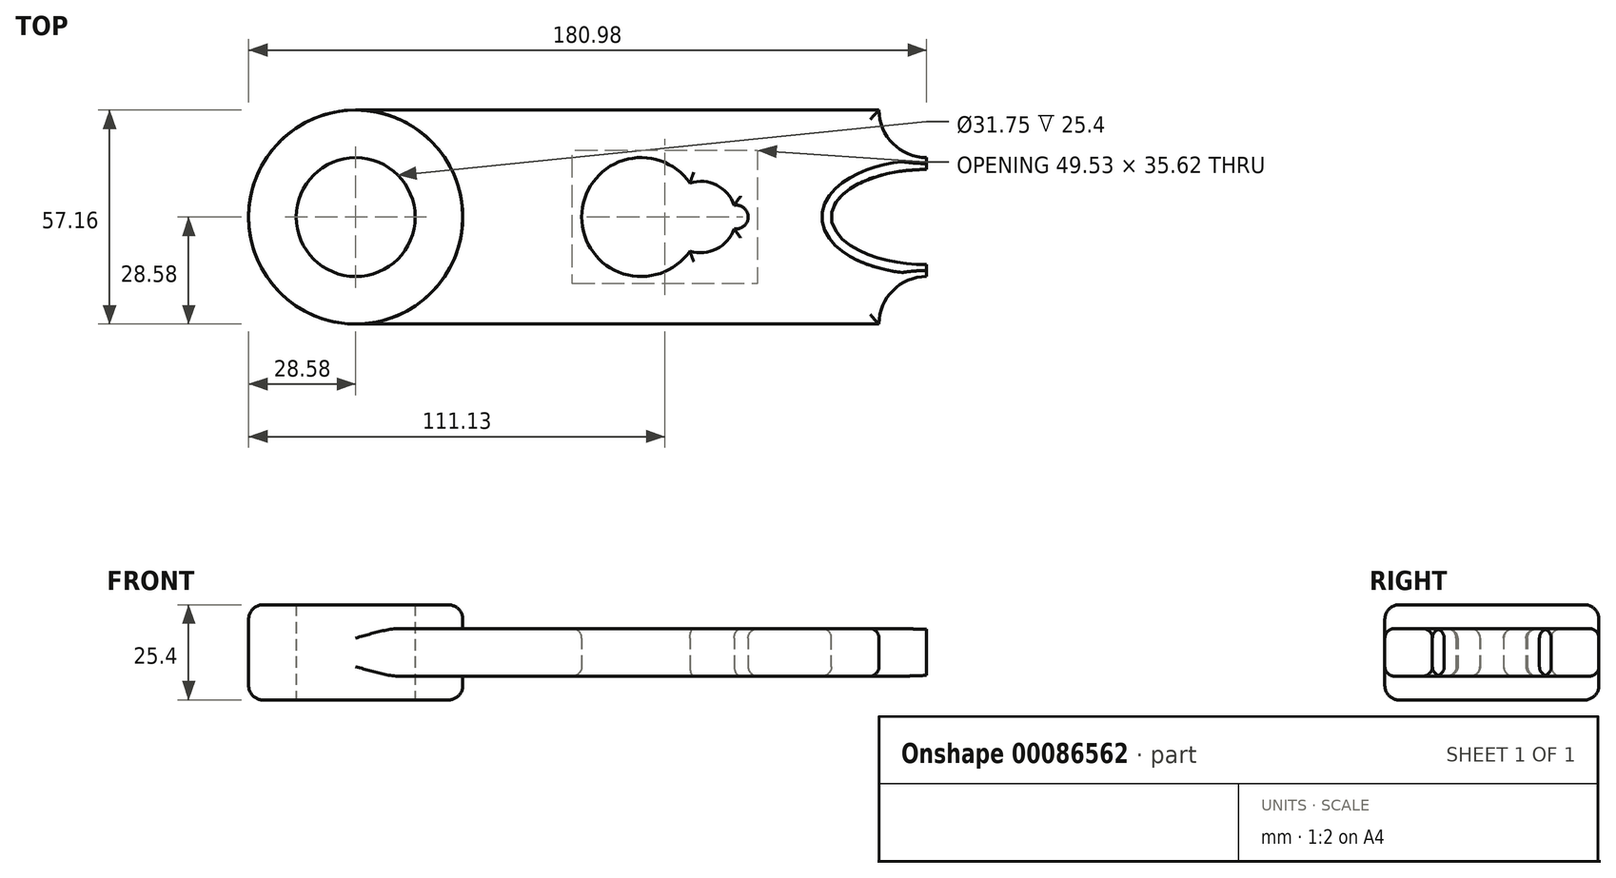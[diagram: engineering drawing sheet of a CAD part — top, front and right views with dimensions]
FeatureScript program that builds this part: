
annotation { "Feature Type Name" : "Feature", "Feature Type Description" : "" }
export const myFeature = defineFeature(function(context is Context, id is Id, definition is map)
    precondition{}
    {
        {
            var Q0;
            Q0=qCreatedBy(makeId("Top.planeOp"),FACE);
            var sketch = newSketch(context, id + "F0", { "sketchPlane" : qUnion([Q0])});
            skLineSegment(sketch, "E0.bottom", {"start": v(76.2, 28.58) * mm, "end": v(-76.2, 28.58) * mm});
            skLineSegment(sketch, "E0.top", {"start": v(76.2, -28.58) * mm, "end": v(-76.2, -28.58) * mm});
            skLineSegment(sketch, "E0.left", {"start": v(76.2, 28.58) * mm, "end": v(76.2, -28.58) * mm});
            skLineSegment(sketch, "E0.right", {"start": v(-76.2, 28.58) * mm, "end": v(-76.2, -28.58) * mm});
            skPoint(sketch, "E0.middle", {"position": v(0, 0) * mm});
            skCircle(sketch, "E1", {"center": v(-76.2, 0) * mm, "radius": 28.58 * mm});
            skCircle(sketch, "E2", {"center": v(-76.2, 0) * mm, "radius": 15.88 * mm});
            skCircle(sketch, "E3", {"center": v(76.2, 28.58) * mm, "radius": 12.7 * mm});
            skCircle(sketch, "E4", {"center": v(76.2, -28.58) * mm, "radius": 12.7 * mm});
            skCircle(sketch, "E5", {"center": v(0, 0) * mm, "radius": 15.88 * mm});
            skCircle(sketch, "E6", {"center": v(15.88, 0) * mm, "radius": 9.53 * mm});
            skCircle(sketch, "E7", {"center": v(25.4, 0) * mm, "radius": 3.18 * mm});
            skEllipse(sketch, "E8", {"center": v(76.2, 0) * mm, "majorRadius": 25.4 * mm, "minorRadius": 12.7 * mm, "majorAxis": v(-1, 0)});
            skSolve(sketch);
        }
        {
            var Q0;
            {var subQ6=sQuery(id+"F0.wireOp",EDGE,"E3");var subQ7=sQuery(id+"F0.wireOp",EDGE,"E0.left");var subQ8=makeQuery(id+"F0.imprint","INTERSECT",VERTEX,{"derivedFrom":[subQ7,subQ6]});Q0=makeQuery(id+"F0.imprint","IMPRINT",FACE,{"disambiguationData":[TD([[makeQuery(id+"F0.imprint","IMPRINT",EDGE,{"disambiguationData":[TD([[subQ8,-1.0]])],"derivedFrom":subQ7}),-1.0]])]});}
            extrude(context, id + "F1", {"entities" : qUnion([Q0]), "endBound" : BoundingType.SYMMETRIC, "depth" : 12.7 * mm});
        }
        {
            var Q0;
            {var subQ1=sQuery(id+"F0.wireOp",EDGE,"E0.right");var subQ3=sQuery(id+"F0.wireOp",EDGE,"E2");var subQ4=makeQuery(id+"F0.imprint","INTERSECT",VERTEX,{"disambiguationData":[OD(0.0)],"derivedFrom":[subQ1,subQ3]});Q0=makeQuery(id+"F0.imprint","IMPRINT",FACE,{"disambiguationData":[TD([[makeQuery(id+"F0.imprint","IMPRINT",EDGE,{"disambiguationData":[TD([[subQ4,-1.0]])],"derivedFrom":subQ3}),-1.0]])]});}
            var Q1;
            {var subQ1=sQuery(id+"F0.wireOp",EDGE,"E0.right");var subQ3=sQuery(id+"F0.wireOp",EDGE,"E2");var subQ4=makeQuery(id+"F0.imprint","INTERSECT",VERTEX,{"disambiguationData":[OD(0.0)],"derivedFrom":[subQ1,subQ3]});Q1=makeQuery(id+"F0.imprint","IMPRINT",FACE,{"disambiguationData":[TD([[makeQuery(id+"F0.imprint","IMPRINT",EDGE,{"disambiguationData":[TD([[subQ4,1.0]])],"derivedFrom":subQ3}),-1.0]])]});}
            extrude(context, id + "F2", {"entities" : qUnion([Q0, Q1]), "operationType" : NewBodyOperationType.ADD, "endBound" : BoundingType.SYMMETRIC, "depth" : 25.4 * mm});
        }
        {
            var Q0;
            Q0=makeQuery(id+"F1.opExtrude","CAP_EDGE",EDGE,{"disambiguationData":[OSD([sQuery(id+"F0.wireOp",EDGE,"E1")])],"isStart":false});
            var Q1;
            Q1=makeQuery(id+"F1.opExtrude","CAP_EDGE",EDGE,{"disambiguationData":[OSD([sQuery(id+"F0.wireOp",EDGE,"E1")])],"isStart":true});
            var Q2;
            Q2=makeQuery(id+"F1.opExtrude","CAP_EDGE",EDGE,{"disambiguationData":[OSD([sQuery(id+"F0.wireOp",EDGE,"E5")])],"isStart":true});
            var Q3;
            {var subQ0=sQuery(id+"F0.wireOp",EDGE,"E6");Q3=makeQuery(id+"F1.opExtrude","CAP_EDGE",EDGE,{"disambiguationData":[OSD([subQ0]),TDD([makeQuery(id+"F0.imprint","IMPRINT",EDGE,{"disambiguationData":[TD([[makeQuery(id+"F0.imprint","INTERSECT",VERTEX,{"disambiguationData":[OD(1.0)],"derivedFrom":[sQuery(id+"F0.wireOp",EDGE,"E5"),subQ0]}),-1.0]])],"derivedFrom":subQ0})])],"isStart":true});}
            var Q4;
            {var subQ0=sQuery(id+"F0.wireOp",EDGE,"E6");Q4=makeQuery(id+"F1.opExtrude","CAP_EDGE",EDGE,{"disambiguationData":[OSD([subQ0]),TDD([makeQuery(id+"F0.imprint","IMPRINT",EDGE,{"disambiguationData":[TD([[makeQuery(id+"F0.imprint","INTERSECT",VERTEX,{"disambiguationData":[OD(0.0)],"derivedFrom":[sQuery(id+"F0.wireOp",EDGE,"E5"),subQ0]}),1.0]])],"derivedFrom":subQ0})])],"isStart":true});}
            var Q5;
            Q5=makeQuery(id+"F1.opExtrude","CAP_EDGE",EDGE,{"disambiguationData":[OSD([sQuery(id+"F0.wireOp",EDGE,"E7")])],"isStart":true});
            var Q6;
            Q6=makeQuery(id+"F1.opExtrude","CAP_EDGE",EDGE,{"disambiguationData":[OSD([sQuery(id+"F0.wireOp",EDGE,"E5")])],"isStart":false});
            var Q7;
            {var subQ0=sQuery(id+"F0.wireOp",EDGE,"E6");Q7=makeQuery(id+"F1.opExtrude","CAP_EDGE",EDGE,{"disambiguationData":[OSD([subQ0]),TDD([makeQuery(id+"F0.imprint","IMPRINT",EDGE,{"disambiguationData":[TD([[makeQuery(id+"F0.imprint","INTERSECT",VERTEX,{"disambiguationData":[OD(0.0)],"derivedFrom":[sQuery(id+"F0.wireOp",EDGE,"E5"),subQ0]}),1.0]])],"derivedFrom":subQ0})])],"isStart":false});}
            var Q8;
            {var subQ0=sQuery(id+"F0.wireOp",EDGE,"E6");Q8=makeQuery(id+"F1.opExtrude","CAP_EDGE",EDGE,{"disambiguationData":[OSD([subQ0]),TDD([makeQuery(id+"F0.imprint","IMPRINT",EDGE,{"disambiguationData":[TD([[makeQuery(id+"F0.imprint","INTERSECT",VERTEX,{"disambiguationData":[OD(1.0)],"derivedFrom":[sQuery(id+"F0.wireOp",EDGE,"E5"),subQ0]}),-1.0]])],"derivedFrom":subQ0})])],"isStart":false});}
            var Q9;
            Q9=makeQuery(id+"F1.opExtrude","CAP_EDGE",EDGE,{"disambiguationData":[OSD([sQuery(id+"F0.wireOp",EDGE,"E7")])],"isStart":false});
            fillet(context, id + "F3", {"entities" : qUnion([Q0, Q1, Q2, Q3, Q4, Q5, Q6, Q7, Q8, Q9]), "radius" : 2.54 * mm, "tangentPropagation" : true, "allowEdgeOverflow" : false});
        }
        {
            var Q0;
            Q0=makeQuery(id+"F2.opExtrude","CAP_EDGE",EDGE,{"disambiguationData":[OSD([sQuery(id+"F0.wireOp",EDGE,"E1")])],"isStart":false});
            var Q1;
            Q1=makeQuery(id+"F2.opExtrude","CAP_EDGE",EDGE,{"disambiguationData":[OSD([sQuery(id+"F0.wireOp",EDGE,"E1")])],"isStart":true});
            fillet(context, id + "F4", {"entities" : qUnion([Q0, Q1]), "radius" : 3.8 * mm, "tangentPropagation" : true, "allowEdgeOverflow" : false});
        }
        {
            var Q0;
            Q0=makeQuery(id+"F1.opExtrude","CAP_EDGE",EDGE,{"disambiguationData":[OSD([sQuery(id+"F0.wireOp",EDGE,"E0.bottom")])],"isStart":false});
            var Q1;
            Q1=makeQuery(id+"F1.opExtrude","CAP_EDGE",EDGE,{"disambiguationData":[OSD([sQuery(id+"F0.wireOp",EDGE,"E3")])],"isStart":false});
            var Q2;
            Q2=makeQuery(id+"F1.opExtrude","CAP_EDGE",EDGE,{"disambiguationData":[OSD([sQuery(id+"F0.wireOp",EDGE,"E8")])],"isStart":false});
            var Q3;
            Q3=makeQuery(id+"F1.opExtrude","CAP_EDGE",EDGE,{"disambiguationData":[OSD([sQuery(id+"F0.wireOp",EDGE,"E4")])],"isStart":false});
            var Q4;
            Q4=makeQuery(id+"F1.opExtrude","CAP_EDGE",EDGE,{"disambiguationData":[OSD([sQuery(id+"F0.wireOp",EDGE,"E0.top")])],"isStart":false});
            var Q5;
            Q5=makeQuery(id+"F1.opExtrude","CAP_EDGE",EDGE,{"disambiguationData":[OSD([sQuery(id+"F0.wireOp",EDGE,"E4")])],"isStart":true});
            var Q6;
            Q6=makeQuery(id+"F1.opExtrude","CAP_EDGE",EDGE,{"disambiguationData":[OSD([sQuery(id+"F0.wireOp",EDGE,"E8")])],"isStart":true});
            var Q7;
            Q7=makeQuery(id+"F1.opExtrude","CAP_EDGE",EDGE,{"disambiguationData":[OSD([sQuery(id+"F0.wireOp",EDGE,"E0.top")])],"isStart":true});
            var Q8;
            Q8=makeQuery(id+"F1.opExtrude","CAP_EDGE",EDGE,{"disambiguationData":[OSD([sQuery(id+"F0.wireOp",EDGE,"E0.bottom")])],"isStart":true});
            var Q9;
            Q9=makeQuery(id+"F1.opExtrude","CAP_EDGE",EDGE,{"disambiguationData":[OSD([sQuery(id+"F0.wireOp",EDGE,"E3")])],"isStart":true});
            fillet(context, id + "F5", {"entities" : qUnion([Q0, Q1, Q2, Q3, Q4, Q5, Q6, Q7, Q8, Q9]), "radius" : 2.54 * mm, "tangentPropagation" : true, "allowEdgeOverflow" : false});
        }
    });
